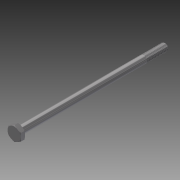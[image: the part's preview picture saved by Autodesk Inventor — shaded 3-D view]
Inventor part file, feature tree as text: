
AUTODESK INVENTOR PART (.ipt)
format: ipt  version: 2013 (Build 170138000, 138)  size: 342,528 bytes
history: native  units: in
note: dims shown in document units (in); Inventor stores cm internally (conversion verified against a paired STEP export)
features: extrude x1, other x1, imported_body x1
ambient origin geometry x8: Origin, YZ Plane, XZ Plane, XY Plane, X Axis, Y Axis, Z Axis, Center Point
feature tree (3):
  extrude  "Extrude14"  [1 undecoded]
  other  "91257A5601"
  imported_body  "Base1"
note: 1 required parameter value undecoded (feature->parameter linkage not recoverable at this tier; creation-order binding heuristic only, values carry confidence <= 0.55)
